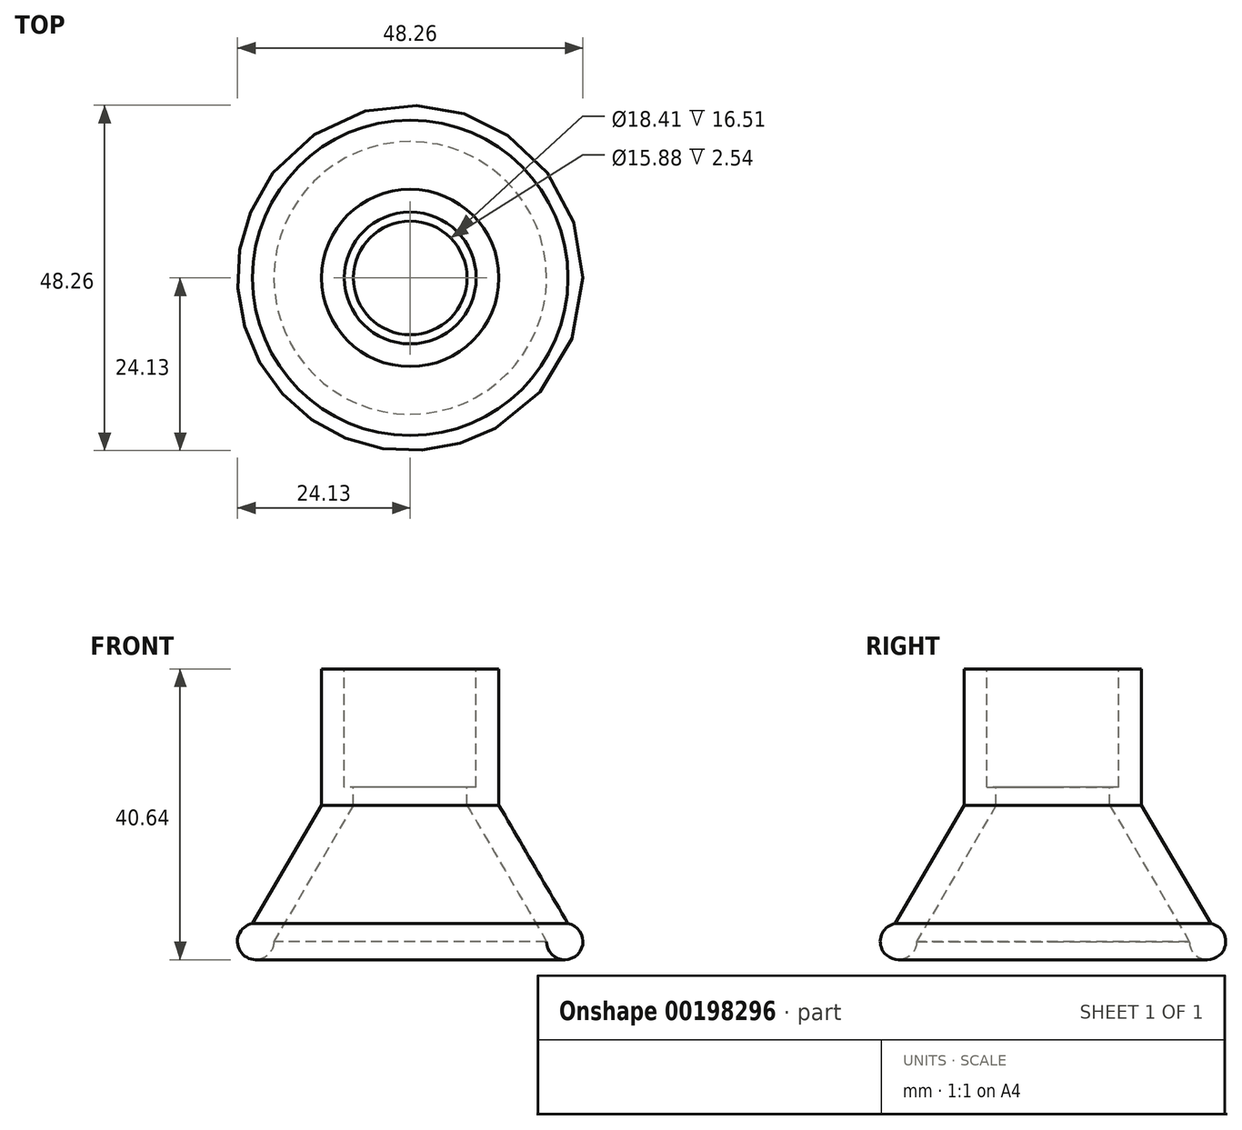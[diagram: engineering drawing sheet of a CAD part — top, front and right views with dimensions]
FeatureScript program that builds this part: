
annotation { "Feature Type Name" : "Feature", "Feature Type Description" : "" }
export const myFeature = defineFeature(function(context is Context, id is Id, definition is map)
    precondition{}
    {
        {
            var Q0;
            Q0=qCreatedBy(makeId("Front.planeOp"),FACE);
            var sketch = newSketch(context, id + "F0", { "sketchPlane" : qUnion([Q0])});
            skLineSegment(sketch, "E0", {"start": v(9.2, 2.54) * mm, "end": v(9.2, 19.05) * mm});
            skLineSegment(sketch, "E1", {"start": v(9.2, 19.05) * mm, "end": v(12.38, 19.05) * mm});
            skLineSegment(sketch, "E2", {"start": v(12.38, 19.05) * mm, "end": v(12.38, 0) * mm});
            skLineSegment(sketch, "E3", {"start": v(12.38, 0) * mm, "end": v(22.04, -16.55) * mm});
            skLineSegment(sketch, "E4", {"start": v(7.94, 0) * mm, "end": v(19.05, -19.05) * mm});
            skArc(sketch, "E5", {"start": v(19.05, -19.05) * mm, "mid": v(23.22, -21) * mm, "end": v(22.04, -16.55) * mm});
            skLineSegment(sketch, "E6", {"start": v(7.94, 0) * mm, "end": v(7.94, 2.54) * mm});
            skLineSegment(sketch, "E7", {"start": v(7.94, 2.54) * mm, "end": v(9.2, 2.54) * mm});
            skLineSegment(sketch, "E8", {"start": v(0, 32.7) * mm, "end": v(0, -44.38) * mm, "construction": true});
            skSolve(sketch);
        }
        {
            var Q0;
            {var subQ0=sQuery(id+"F0.wireOp",EDGE,"E1");Q0=makeQuery(id+"F0.imprint","IMPRINT",FACE,{"disambiguationData":[TD([[makeQuery(id+"F0.imprint","IMPRINT",EDGE,{"derivedFrom":subQ0}),-1.0]])]});}
            var Q1;
            {var subQ0=sQuery(id+"F0.wireOp",EDGE,"NsCxnYeu-V2wK-AO4W-kreo-k2jRx2hmMsw9");Q1=makeQuery(id+"F0.imprint","IMPRINT",FACE,{"disambiguationData":[TD([[makeQuery(id+"F0.imprint","IMPRINT",EDGE,{"derivedFrom":subQ0}),-1.0]])]});}
            var Q2;
            Q2=sQuery(id+"F0.wireOp",EDGE,"E8");
            revolve(context, id + "F1", {"entities" : qUnion([Q0, Q1]), "axis" : qUnion([Q2]), "revolveType" : RevolveType.FULL});
        }
    });
